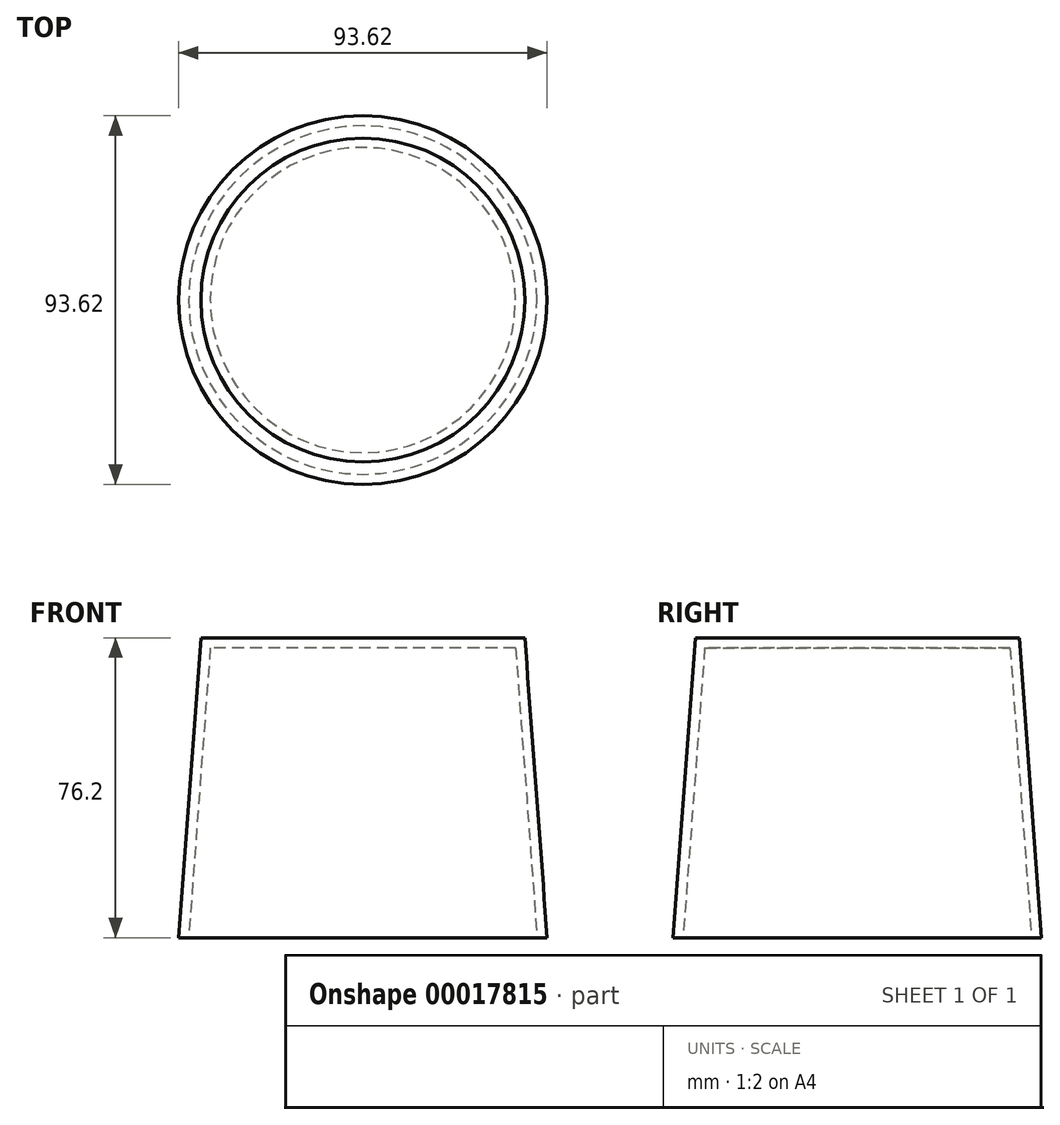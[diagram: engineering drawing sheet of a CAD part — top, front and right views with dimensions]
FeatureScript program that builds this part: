
annotation { "Feature Type Name" : "Feature", "Feature Type Description" : "" }
export const myFeature = defineFeature(function(context is Context, id is Id, definition is map)
    precondition{}
    {
        {
            var Q0;
            Q0=qCreatedBy(makeId("Top.planeOp"),FACE);
            cPlane(context, id + "F0", {"entities" : qUnion([Q0]), "cplaneType" : CPlaneType.OFFSET, "offset" : 76.2 * mm, "oppositeDirection" : true, "width" : 152.4 * mm, "height" : 152.4 * mm});
        }
        {
            var Q0;
            Q0=qCreatedBy(makeId("Top.planeOp"),FACE);
            var sketch = newSketch(context, id + "F1", { "sketchPlane" : qUnion([Q0])});
            skCircle(sketch, "E0", {"center": v(0, 0) * mm, "radius": 41.14 * mm});
            skSolve(sketch);
        }
        {
            var Q0;
            Q0=qCreatedBy(id+"F0.planeOp",FACE);
            var sketch = newSketch(context, id + "F2", { "sketchPlane" : qUnion([Q0])});
            skCircle(sketch, "E1", {"center": v(0, 0) * mm, "radius": 46.8 * mm});
            skSolve(sketch);
        }
        {
            var Q0;
            Q0=makeQuery(id+"F1.imprint","IMPRINT",FACE,{"disambiguationData":[TD([[makeQuery(id+"F1.imprint","IMPRINT",EDGE,{"derivedFrom":sQuery(id+"F1.wireOp",EDGE,"E0")}),1.0]])]});
            var Q1;
            Q1=makeQuery(id+"F2.imprint","IMPRINT",FACE,{"disambiguationData":[TD([[makeQuery(id+"F2.imprint","IMPRINT",EDGE,{"derivedFrom":sQuery(id+"F2.wireOp",EDGE,"E1")}),1.0]])]});
            loft(context, id + "F3", {"sheetProfilesArray" : [{ "sheetProfileEntities" : qUnion([Q0]) }, { "sheetProfileEntities" : qUnion([Q1]) }]});
        }
        {
            var Q0;
            Q0=makeQuery(id+"F3.opLoft","CAP_FACE",FACE,{"disambiguationData":[OSD([makeQuery(id+"F2.imprint","IMPRINT",FACE,{"disambiguationData":[TD([[makeQuery(id+"F2.imprint","IMPRINT",EDGE,{"derivedFrom":sQuery(id+"F2.wireOp",EDGE,"E1")}),1.0]])]})])],"isStart":true});
            shell(context, id + "F4", {"entities" : qUnion([Q0]), "thickness" : 2.54 * mm});
        }
    });
